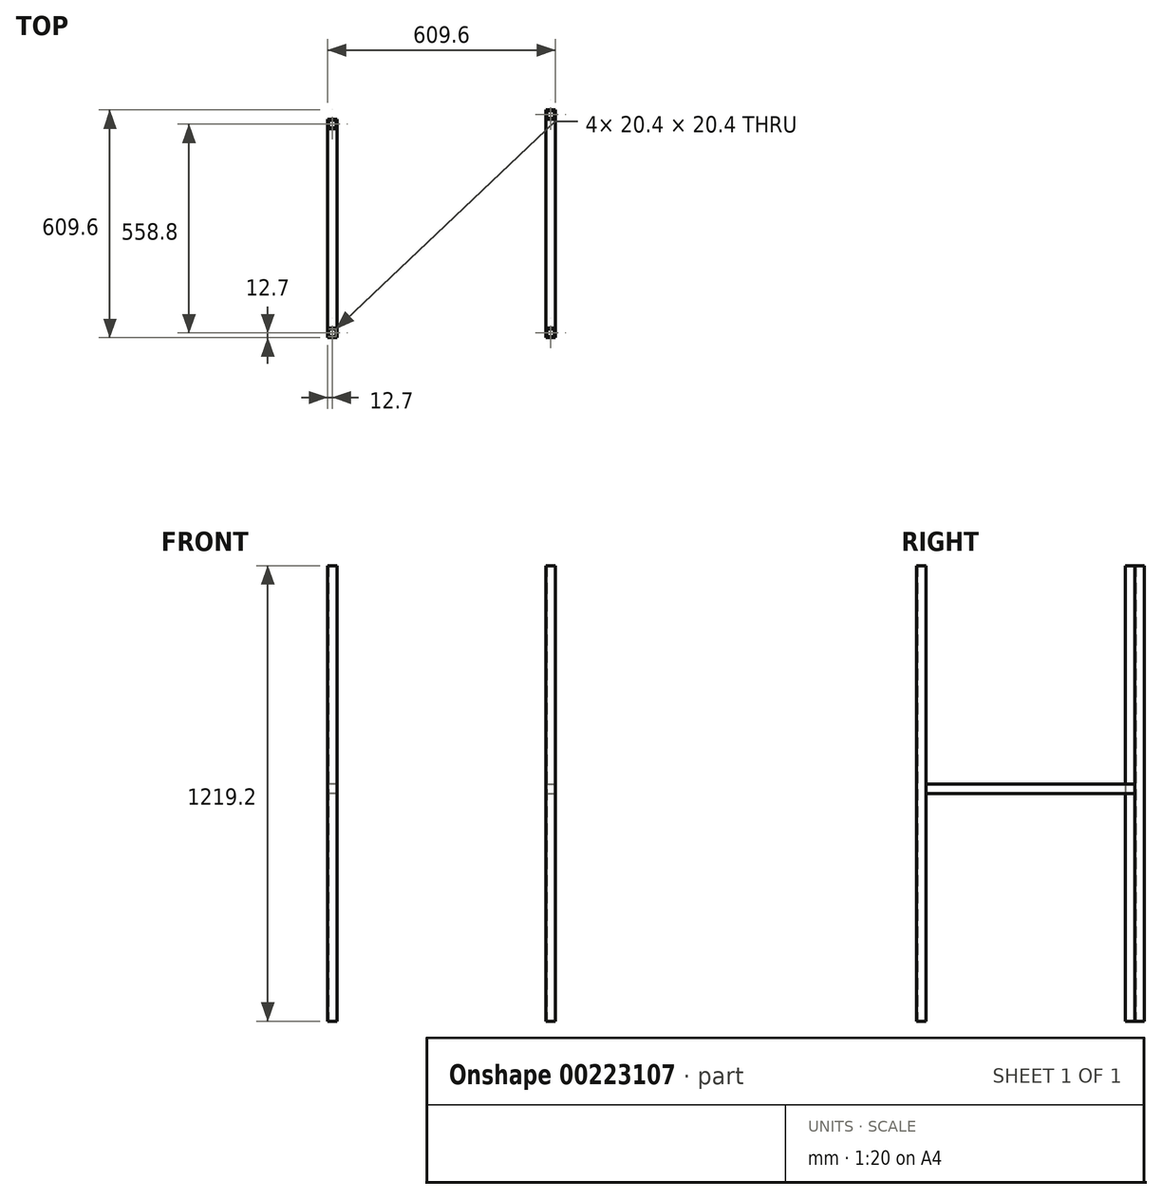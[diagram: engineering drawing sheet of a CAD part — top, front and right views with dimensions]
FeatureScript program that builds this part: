
annotation { "Feature Type Name" : "Feature", "Feature Type Description" : "" }
export const myFeature = defineFeature(function(context is Context, id is Id, definition is map)
    precondition{}
    {
        {
            var Q0;
            Q0=qCreatedBy(makeId("Top.planeOp"),FACE);
            var sketch = newSketch(context, id + "F0", { "sketchPlane" : qUnion([Q0])});
            skLineSegment(sketch, "E0.bottom", {"start": v(-12.7, 12.7) * mm, "end": v(12.7, 12.7) * mm});
            skLineSegment(sketch, "E0.top", {"start": v(-12.7, -12.7) * mm, "end": v(12.7, -12.7) * mm});
            skLineSegment(sketch, "E0.left", {"start": v(-12.7, 12.7) * mm, "end": v(-12.7, -12.7) * mm});
            skLineSegment(sketch, "E0.right", {"start": v(12.7, 12.7) * mm, "end": v(12.7, -12.7) * mm});
            skPoint(sketch, "E0.middle", {"position": v(0, 0) * mm});
            skLineSegment(sketch, "E1.0", {"start": v(-10.2, 10.2) * mm, "end": v(10.2, 10.2) * mm});
            skLineSegment(sketch, "E2.0", {"start": v(10.2, 10.2) * mm, "end": v(10.2, -10.2) * mm});
            skLineSegment(sketch, "E2.1", {"start": v(-10.2, -10.2) * mm, "end": v(10.2, -10.2) * mm});
            skLineSegment(sketch, "E2.2", {"start": v(-10.2, 10.2) * mm, "end": v(-10.2, -10.2) * mm});
            skLineSegment(sketch, "E3.bottom", {"start": v(-12.7, -571.5) * mm, "end": v(12.7, -571.5) * mm});
            skLineSegment(sketch, "E3.top", {"start": v(-12.7, -596.9) * mm, "end": v(12.7, -596.9) * mm});
            skLineSegment(sketch, "E3.left", {"start": v(-12.7, -571.5) * mm, "end": v(-12.7, -596.9) * mm});
            skLineSegment(sketch, "E3.right", {"start": v(12.7, -571.5) * mm, "end": v(12.7, -596.9) * mm});
            skPoint(sketch, "E3.middle", {"position": v(0, -584.2) * mm});
            skLineSegment(sketch, "E4.0", {"start": v(-10.2, -574) * mm, "end": v(10.2, -574) * mm});
            skLineSegment(sketch, "E5.0", {"start": v(10.2, -574) * mm, "end": v(10.2, -594.4) * mm});
            skLineSegment(sketch, "E5.1", {"start": v(-10.2, -594.4) * mm, "end": v(10.2, -594.4) * mm});
            skLineSegment(sketch, "E5.2", {"start": v(-10.2, -574) * mm, "end": v(-10.2, -594.4) * mm});
            skLineSegment(sketch, "E6", {"start": v(12.7, -12.7) * mm, "end": v(12.7, -596.9) * mm});
            skLineSegment(sketch, "E7", {"start": v(12.7, -596.9) * mm, "end": v(-596.9, -596.9) * mm});
            skLineSegment(sketch, "E8", {"start": v(-596.9, -596.9) * mm, "end": v(-596.9, -12.7) * mm});
            skLineSegment(sketch, "E9.bottom", {"start": v(-596.9, -571.5) * mm, "end": v(-571.5, -571.5) * mm});
            skLineSegment(sketch, "E9.top", {"start": v(-596.9, -596.9) * mm, "end": v(-571.5, -596.9) * mm});
            skLineSegment(sketch, "E9.left", {"start": v(-596.9, -571.5) * mm, "end": v(-596.9, -596.9) * mm});
            skLineSegment(sketch, "E9.right", {"start": v(-571.5, -571.5) * mm, "end": v(-571.5, -596.9) * mm});
            skPoint(sketch, "E9.middle", {"position": v(-584.2, -584.2) * mm});
            skLineSegment(sketch, "E10.0", {"start": v(-594.4, -574) * mm, "end": v(-574, -574) * mm});
            skLineSegment(sketch, "E11.0", {"start": v(-574, -574) * mm, "end": v(-574, -594.4) * mm});
            skLineSegment(sketch, "E11.1", {"start": v(-594.4, -594.4) * mm, "end": v(-574, -594.4) * mm});
            skLineSegment(sketch, "E11.2", {"start": v(-594.4, -574) * mm, "end": v(-594.4, -594.4) * mm});
            skLineSegment(sketch, "E12.bottom", {"start": v(-596.9, -12.7) * mm, "end": v(-571.5, -12.7) * mm});
            skLineSegment(sketch, "E12.top", {"start": v(-596.9, -38.1) * mm, "end": v(-571.5, -38.1) * mm});
            skLineSegment(sketch, "E12.left", {"start": v(-596.9, -12.7) * mm, "end": v(-596.9, -38.1) * mm});
            skLineSegment(sketch, "E12.right", {"start": v(-571.5, -12.7) * mm, "end": v(-571.5, -38.1) * mm});
            skPoint(sketch, "E12.middle", {"position": v(-584.2, -25.4) * mm});
            skLineSegment(sketch, "E13.0", {"start": v(-594.4, -15.2) * mm, "end": v(-574, -15.2) * mm});
            skLineSegment(sketch, "E14.0", {"start": v(-574, -15.2) * mm, "end": v(-574, -35.6) * mm});
            skLineSegment(sketch, "E14.1", {"start": v(-594.4, -35.6) * mm, "end": v(-574, -35.6) * mm});
            skLineSegment(sketch, "E14.2", {"start": v(-594.4, -15.2) * mm, "end": v(-594.4, -35.6) * mm});
            skSolve(sketch);
        }
        {
            var Q0;
            Q0 = qSketchRegion(id + "F0", true);
            extrude(context, id + "F1", {"entities" : qUnion([Q0]), "depth" : 1219.2 * mm});
        }
        {
            var Q0;
            Q0=makeQuery(id+"F1.opExtrude","SWEPT_FACE",FACE,{"disambiguationData":[OSD([sQuery(id+"F0.wireOp",EDGE,"E0.top")])]});
            var sketch = newSketch(context, id + "F2", { "sketchPlane" : qUnion([Q0])});
            skLineSegment(sketch, "E15.bottom", {"start": v(-12.7, 635) * mm, "end": v(12.7, 635) * mm});
            skLineSegment(sketch, "E15.top", {"start": v(-12.7, 609.6) * mm, "end": v(12.7, 609.6) * mm});
            skLineSegment(sketch, "E15.left", {"start": v(-12.7, 635) * mm, "end": v(-12.7, 609.6) * mm});
            skLineSegment(sketch, "E15.right", {"start": v(12.7, 635) * mm, "end": v(12.7, 609.6) * mm});
            skLineSegment(sketch, "E16", {"start": v(-12.7, 635) * mm, "end": v(-571.5, 635) * mm});
            skLineSegment(sketch, "E17.0", {"start": v(-571.5, 1219.2) * mm, "end": v(-571.5, 0) * mm});
            skLineSegment(sketch, "E18.bottom", {"start": v(-571.5, 635) * mm, "end": v(-596.9, 635) * mm});
            skLineSegment(sketch, "E18.top", {"start": v(-571.5, 609.6) * mm, "end": v(-596.9, 609.6) * mm});
            skLineSegment(sketch, "E18.left", {"start": v(-571.5, 635) * mm, "end": v(-571.5, 609.6) * mm});
            skLineSegment(sketch, "E18.right", {"start": v(-596.9, 635) * mm, "end": v(-596.9, 609.6) * mm});
            skSolve(sketch);
        }
        {
            var Q0;
            Q0 = qSketchRegion(id + "F2", true);
            extrude(context, id + "F3", {"entities" : qUnion([Q0]), "depth" : 558.8 * mm});
        }
    });
